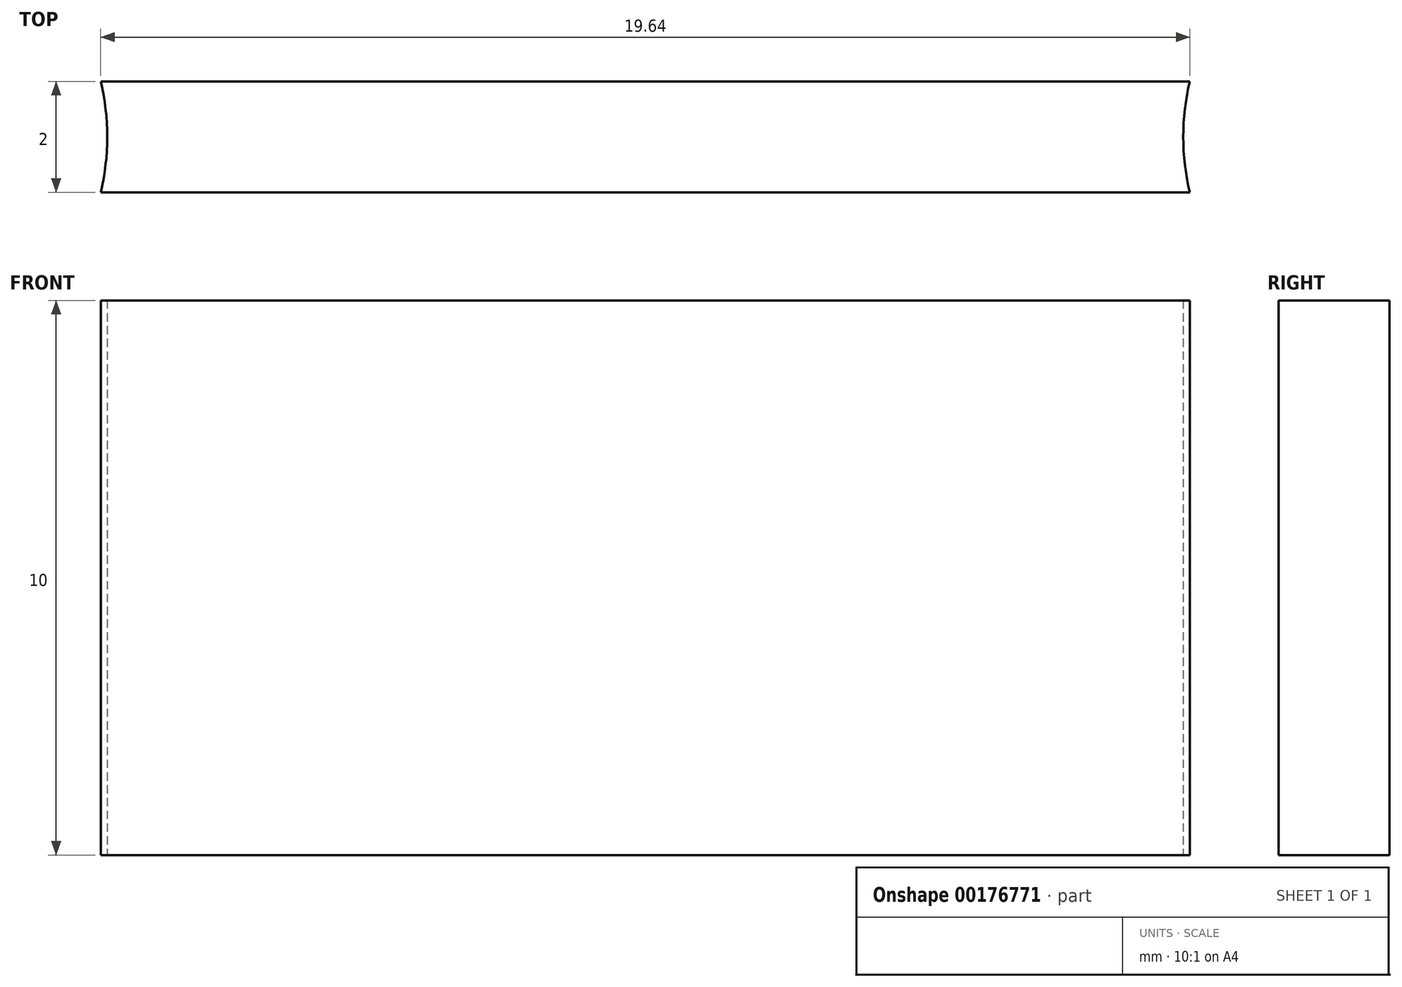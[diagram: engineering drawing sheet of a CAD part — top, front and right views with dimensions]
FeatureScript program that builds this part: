
annotation { "Feature Type Name" : "Feature", "Feature Type Description" : "" }
export const myFeature = defineFeature(function(context is Context, id is Id, definition is map)
    precondition{}
    {
        {
            var Q0;
            Q0=qCreatedBy(makeId("Top.planeOp"),FACE);
            var sketch = newSketch(context, id + "F0", { "sketchPlane" : qUnion([Q0])});
            skCircle(sketch, "E0", {"center": v(-14, 0) * mm, "radius": 2.5 * mm});
            skCircle(sketch, "E1", {"center": v(14, 0) * mm, "radius": 2.5 * mm});
            skCircle(sketch, "E2.0", {"center": v(-14, 0) * mm, "radius": 4.3 * mm});
            skCircle(sketch, "E3.0", {"center": v(14, 0) * mm, "radius": 4.3 * mm});
            skLineSegment(sketch, "E4", {"start": v(-14, 0) * mm, "end": v(14, 0) * mm, "construction": true});
            skPoint(sketch, "E5.middle", {"position": v(0, 0) * mm});
            skLineSegment(sketch, "E6", {"start": v(-9.82, 1) * mm, "end": v(9.82, 1) * mm});
            skLineSegment(sketch, "E7", {"start": v(-9.82, -1) * mm, "end": v(9.82, -1) * mm});
            skLineSegment(sketch, "E8", {"start": v(0, 1) * mm, "end": v(0, 0) * mm});
            skLineSegment(sketch, "E9", {"start": v(0, 0) * mm, "end": v(0, -1) * mm});
            skSolve(sketch);
        }
        {
            var Q0;
            {var subQ0=sQuery(id+"F0.wireOp",EDGE,"E8");Q0=makeQuery(id+"F0.imprint","IMPRINT",FACE,{"disambiguationData":[TD([[makeQuery(id+"F0.imprint","IMPRINT",EDGE,{"derivedFrom":subQ0}),-1.0]])]});}
            var Q1;
            {var subQ0=sQuery(id+"F0.wireOp",EDGE,"E8");Q1=makeQuery(id+"F0.imprint","IMPRINT",FACE,{"disambiguationData":[TD([[makeQuery(id+"F0.imprint","IMPRINT",EDGE,{"derivedFrom":subQ0}),1.0]])]});}
            extrude(context, id + "F1", {"entities" : qUnion([Q0, Q1]), "depth" : 10 * mm});
        }
    });
